# Revit family: AD-S12 - Yoke Mount
name_source: partatom
category: Generic Models
revit_build: Autodesk Revit Architecture 2012 (Build: 20110309_2315(x64)
units: mm (PartAtom-declared; Revit-internal decimal feet)

## types (1)
- AD-S12 - Yoke Mount
    100V Taps = 100, 50, 25
    70V Taps = 100, 50, 25, 12.5
    Coverage Horizontal = 90.00°
    Coverage Vertical = 90.00°
    Default Elevation = 4' - 0"
    Depth = 0' - 11 23/32"
    Description = 10" 2-Way Surface Mount Loudspeaker
    Height = 1' - 11 15/32"
    Impedance = 8
    Manufacturer = QSC Audio Products, LLC
    Manufacturer URL = www.qscaudio.com
    Model = AD-S10T
    Mount Depth = 0' - 10"
    Mount Height = 1' - 11 15/32"
    Mount Width = 0' - 4 17/32"
    Power Handling = 250
    Product Documentation Link = TBA
    Product Page URL = TBA
    Regulatory Compliance = RoHS
    SPL Max = 122
    Sensitivity = 92
    URL = TBA
    Weight Dimensional (kg) = 18.45
    Weight Dimensional (lb) = 40.6
    Weight Product (kg) = 15
    Weight Product (lb) = 31
    Width = 10' - 0"

## geometry (parser evidence)
native form markers: Blend x1, Sweep x3
no freeform markers — native parametric forms only
